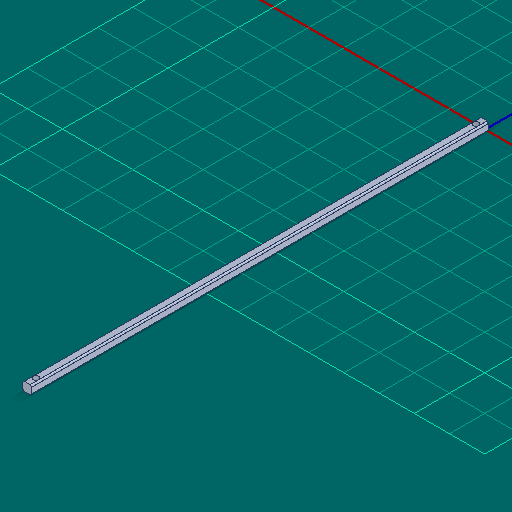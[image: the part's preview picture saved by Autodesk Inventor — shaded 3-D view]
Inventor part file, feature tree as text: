
AUTODESK INVENTOR PART (.ipt)
format: ipt  version: 2025 (Build 290162000, 162)  size: 177,152 bytes
history: native  units: in
note: dims shown in document units (in); Inventor stores cm internally (conversion verified against a paired STEP export)
features: extrude x3, sketch x3, thicken_offset x1, other x1
ambient origin geometry x8: Origin, YZ Plane, XZ Plane, XY Plane, X Axis, Y Axis, Z Axis, Center Point
bodies: Solid1 (feature_tree)
feature tree (8):
  extrude  "Extrusion1"  Depth=12.1875in
  thicken_offset  "Thicken1"
  extrude  "Extrusion2"  Depth=11.125in
  extrude  "Extrusion3"  Depth=0.165in
  sketch  "Sketch2"  dims[d0=0.0625in d1=0.0in d2=12.1875in]
  sketch  "Sketch3"  dims[d3=12.125in d4=11.125in]
  sketch  "Sketch4"  dims[d5=0.0in d6=0.165in d7=0.165in d8=1.0in d9=0.0in]
  other  "Cut-Revolve3"
